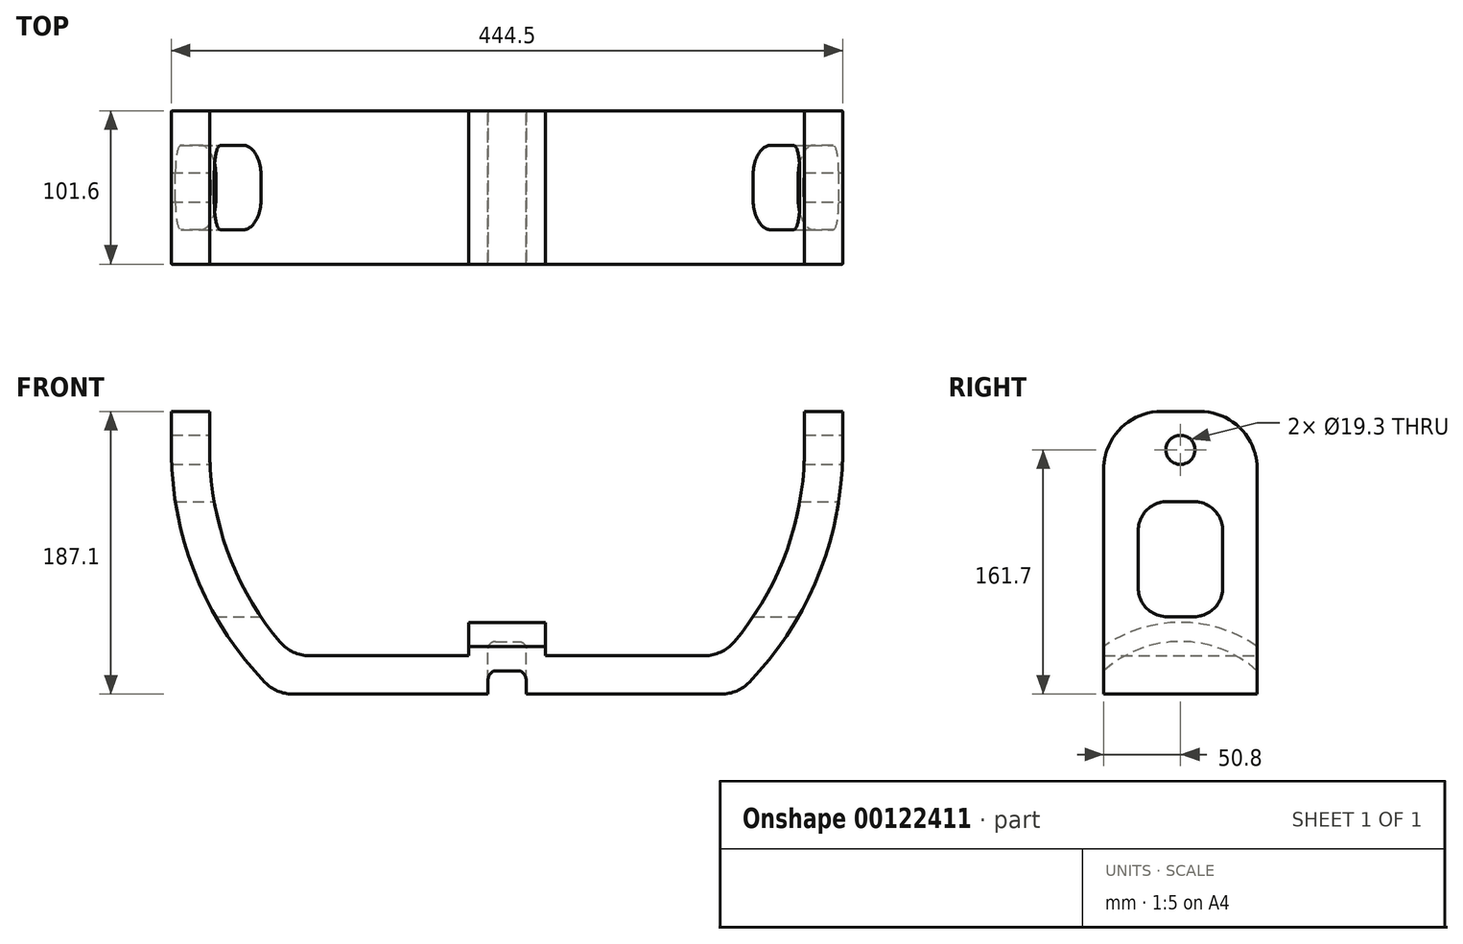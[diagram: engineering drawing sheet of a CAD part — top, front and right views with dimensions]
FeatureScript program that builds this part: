
annotation { "Feature Type Name" : "Feature", "Feature Type Description" : "" }
export const myFeature = defineFeature(function(context is Context, id is Id, definition is map)
    precondition{}
    {
        {
            var Q0;
            Q0=qCreatedBy(makeId("Front.planeOp"),FACE);
            var sketch = newSketch(context, id + "F0", { "sketchPlane" : qUnion([Q0])});
            skArc(sketch, "E0", {"start": v(-196.85, 0) * mm, "mid": v(-182.63, -73.46) * mm, "end": v(-142.03, -136.3) * mm});
            skArc(sketch, "E1.0", {"start": v(-222.25, 0) * mm, "mid": v(-204.06, -88.06) * mm, "end": v(-152.47, -161.7) * mm});
            skLineSegment(sketch, "E2", {"start": v(-196.85, 0) * mm, "end": v(196.85, 0) * mm, "construction": true});
            skLineSegment(sketch, "E3", {"start": v(-112.26, -161.7) * mm, "end": v(112.26, -161.7) * mm});
            skPoint(sketch, "E4", {"position": v(0, -161.7) * mm});
            skLineSegment(sketch, "E5.bottom", {"start": v(7.05, -253.9) * mm, "end": v(-7.05, -253.9) * mm, "construction": true});
            skLineSegment(sketch, "E5.top", {"start": v(7.05, -152.3) * mm, "end": v(-7.05, -152.3) * mm, "construction": true});
            skLineSegment(sketch, "E5.left", {"start": v(7.05, -253.9) * mm, "end": v(7.05, -152.3) * mm, "construction": true});
            skLineSegment(sketch, "E5.right", {"start": v(-7.05, -253.9) * mm, "end": v(-7.05, -152.3) * mm, "construction": true});
            skPoint(sketch, "E5.middle", {"position": v(0, -203.1) * mm});
            skCircle(sketch, "E6", {"center": v(0, 0) * mm, "radius": 254 * mm, "construction": true});
            skLineSegment(sketch, "E7.0", {"start": v(-142.03, -136.3) * mm, "end": v(142.03, -136.3) * mm});
            skLineSegment(sketch, "E8", {"start": v(-112.26, -161.7) * mm, "end": v(-152.47, -161.7) * mm});
            skLineSegment(sketch, "E9", {"start": v(112.26, -161.7) * mm, "end": v(152.47, -161.7) * mm});
            skArc(sketch, "E10.trimOffspring", {"start": v(142.03, -136.3) * mm, "mid": v(182.63, -73.46) * mm, "end": v(196.85, 0) * mm});
            skArc(sketch, "E11.trimOffspring", {"start": v(152.47, -161.7) * mm, "mid": v(204.06, -88.06) * mm, "end": v(222.25, 0) * mm});
            skLineSegment(sketch, "E12", {"start": v(-222.25, 0) * mm, "end": v(-222.25, 25.4) * mm});
            skLineSegment(sketch, "E13", {"start": v(-222.25, 25.4) * mm, "end": v(-196.85, 25.4) * mm});
            skLineSegment(sketch, "E14", {"start": v(-196.85, 25.4) * mm, "end": v(-196.85, 0) * mm});
            skLineSegment(sketch, "E15", {"start": v(196.85, 0) * mm, "end": v(196.85, 25.4) * mm});
            skLineSegment(sketch, "E16", {"start": v(196.85, 25.4) * mm, "end": v(222.25, 25.4) * mm});
            skLineSegment(sketch, "E17", {"start": v(222.25, 25.4) * mm, "end": v(222.25, 0) * mm});
            skLineSegment(sketch, "E18", {"start": v(0, 254) * mm, "end": v(0, -254) * mm, "construction": true});
            skSolve(sketch);
        }
        {
            var Q0;
            Q0 = qSketchRegion(id + "F0", true);
            extrude(context, id + "F1", {"entities" : qUnion([Q0]), "endBound" : BoundingType.SYMMETRIC, "depth" : 101.6 * mm, "offsetDistance" : 25.4 * mm});
        }
        {
            var Q0;
            Q0=makeQuery(id+"F1.opExtrude","SWEPT_EDGE",EDGE,{"disambiguationData":[OSD([sQuery(id+"F0.wireOp",EDGE,"E0"),sQuery(id+"F0.wireOp",EDGE,"E7.0")])]});
            var Q1;
            Q1=makeQuery(id+"F1.opExtrude","SWEPT_EDGE",EDGE,{"disambiguationData":[OSD([sQuery(id+"F0.wireOp",EDGE,"E1.0"),sQuery(id+"F0.wireOp",EDGE,"E8")])]});
            var Q2;
            Q2=makeQuery(id+"F1.opExtrude","SWEPT_EDGE",EDGE,{"disambiguationData":[OSD([sQuery(id+"F0.wireOp",EDGE,"E9"),sQuery(id+"F0.wireOp",EDGE,"E11.trimOffspring")])]});
            var Q3;
            Q3=makeQuery(id+"F1.opExtrude","SWEPT_EDGE",EDGE,{"disambiguationData":[OSD([sQuery(id+"F0.wireOp",EDGE,"E7.0"),sQuery(id+"F0.wireOp",EDGE,"E10.trimOffspring")])]});
            fillet(context, id + "F2", {"entities" : qUnion([Q0, Q1, Q2, Q3]), "tangentPropagation" : true, "radius" : 25.4 * mm, "defaultsChanged" : false, "vertexSettings" : [], "allowEdgeOverflow" : false});
        }
        {
            var Q0;
            Q0=makeQuery(id+"F1.opExtrude","CAP_EDGE",EDGE,{"disambiguationData":[OSD([sQuery(id+"F0.wireOp",EDGE,"E13")])],"isStart":false});
            var Q1;
            Q1=makeQuery(id+"F1.opExtrude","CAP_EDGE",EDGE,{"disambiguationData":[OSD([sQuery(id+"F0.wireOp",EDGE,"E13")])],"isStart":true});
            var Q2;
            Q2=makeQuery(id+"F1.opExtrude","CAP_EDGE",EDGE,{"disambiguationData":[OSD([sQuery(id+"F0.wireOp",EDGE,"E16")])],"isStart":true});
            var Q3;
            Q3=makeQuery(id+"F1.opExtrude","CAP_EDGE",EDGE,{"disambiguationData":[OSD([sQuery(id+"F0.wireOp",EDGE,"E16")])],"isStart":false});
            fillet(context, id + "F3", {"entities" : qUnion([Q0, Q1, Q2, Q3]), "tangentPropagation" : true, "radius" : 38.1 * mm, "defaultsChanged" : true, "vertexSettings" : [], "allowEdgeOverflow" : false});
        }
        {
            var Q0;
            Q0=qCreatedBy(makeId("Right.planeOp"),FACE);
            var sketch = newSketch(context, id + "F4", { "sketchPlane" : qUnion([Q0])});
            skCircle(sketch, "E19", {"center": v(0, 0) * mm, "radius": 9.65 * mm});
            skSolve(sketch);
        }
        {
            var Q0;
            Q0 = qSketchRegion(id + "F4", true);
            extrude(context, id + "F5", {"entities" : qUnion([Q0]), "operationType" : NewBodyOperationType.REMOVE, "endBound" : BoundingType.SYMMETRIC, "oppositeDirection" : true, "depth" : 482.6 * mm, "offsetDistance" : 25.4 * mm});
        }
        {
            var Q0;
            Q0=qCreatedBy(makeId("Right.planeOp"),FACE);
            var sketch = newSketch(context, id + "F6", { "sketchPlane" : qUnion([Q0])});
            skArc(sketch, "E20", {"start": v(50.8, -130.15) * mm, "mid": v(0, -114.2) * mm, "end": v(-50.8, -130.15) * mm});
            skArc(sketch, "E21", {"start": v(63.97, -161.7) * mm, "mid": v(0, -126.9) * mm, "end": v(-63.97, -161.7) * mm});
            skLineSegment(sketch, "E22.0", {"start": v(-50.8, -153.89) * mm, "end": v(-50.8, -130.15) * mm});
            skLineSegment(sketch, "E23.0", {"start": v(-50.8, -161.7) * mm, "end": v(-50.8, -153.89) * mm});
            skLineSegment(sketch, "E24.0", {"start": v(50.8, -161.7) * mm, "end": v(-50.8, -161.7) * mm});
            skLineSegment(sketch, "E25.0", {"start": v(50.8, -153.89) * mm, "end": v(50.8, -161.7) * mm});
            skLineSegment(sketch, "E26.0", {"start": v(50.8, -153.89) * mm, "end": v(50.8, -130.15) * mm});
            skPoint(sketch, "E27.orphan", {"position": v(-50.8, -12.7) * mm});
            skPoint(sketch, "E28.orphan", {"position": v(50.8, -12.7) * mm});
            skSolve(sketch);
        }
        {
            var Q0;
            Q0=qCreatedBy(makeId("Right.planeOp"),FACE);
            var sketch = newSketch(context, id + "F7", { "sketchPlane" : qUnion([Q0])});
            skArc(sketch, "E29.0", {"start": v(50.8, -130.15) * mm, "mid": v(0, -114.2) * mm, "end": v(-50.8, -130.15) * mm});
            skLineSegment(sketch, "E30.0", {"start": v(-50.8, -153.89) * mm, "end": v(-50.8, -130.15) * mm});
            skLineSegment(sketch, "E31.0", {"start": v(-50.8, -161.7) * mm, "end": v(-50.8, -153.89) * mm});
            skLineSegment(sketch, "E32.0", {"start": v(50.8, -161.7) * mm, "end": v(-50.8, -161.7) * mm});
            skLineSegment(sketch, "E33.0", {"start": v(50.8, -153.89) * mm, "end": v(50.8, -130.15) * mm});
            skLineSegment(sketch, "E34.0", {"start": v(50.8, -153.89) * mm, "end": v(50.8, -161.7) * mm});
            skSolve(sketch);
        }
        {
            var Q0;
            Q0 = qSketchRegion(id + "F7", true);
            extrude(context, id + "F8", {"entities" : qUnion([Q0]), "operationType" : NewBodyOperationType.ADD, "endBound" : BoundingType.SYMMETRIC, "depth" : 50.8 * mm, "offsetDistance" : 25.4 * mm});
        }
        {
            var Q0;
            Q0=qCreatedBy(makeId("Right.planeOp"),FACE);
            var sketch = newSketch(context, id + "F9", { "sketchPlane" : qUnion([Q0])});
            skArc(sketch, "E35.0", {"start": v(63.97, -161.7) * mm, "mid": v(0, -126.9) * mm, "end": v(-63.97, -161.7) * mm});
            skLineSegment(sketch, "E36.0", {"start": v(50.8, -161.7) * mm, "end": v(-50.8, -161.7) * mm});
            skLineSegment(sketch, "E37", {"start": v(-63.97, -161.7) * mm, "end": v(-50.8, -161.7) * mm});
            skLineSegment(sketch, "E38", {"start": v(50.8, -161.7) * mm, "end": v(63.97, -161.7) * mm});
            skSolve(sketch);
        }
        {
            var Q0;
            Q0 = qSketchRegion(id + "F9", true);
            extrude(context, id + "F10", {"entities" : qUnion([Q0]), "operationType" : NewBodyOperationType.REMOVE, "endBound" : BoundingType.SYMMETRIC, "oppositeDirection" : true, "depth" : 25.4 * mm, "offsetDistance" : 25.4 * mm});
        }
        {
            var Q0;
            Q0=qCreatedBy(makeId("Right.planeOp"),FACE);
            var sketch = newSketch(context, id + "F11", { "sketchPlane" : qUnion([Q0])});
            skLineSegment(sketch, "E39.bottom", {"start": v(8.89, -110.5) * mm, "end": v(-8.9, -110.5) * mm});
            skLineSegment(sketch, "E39.top", {"start": v(8.9, -34.3) * mm, "end": v(-8.9, -34.3) * mm});
            skLineSegment(sketch, "E39.left", {"start": v(27.94, -91.44) * mm, "end": v(27.94, -53.34) * mm});
            skLineSegment(sketch, "E39.right", {"start": v(-27.94, -91.44) * mm, "end": v(-27.94, -53.34) * mm});
            skPoint(sketch, "E39.middle", {"position": v(0, -72.4) * mm});
            skPoint(sketch, "E40.visualSharp", {"position": v(-27.94, -34.3) * mm});
            skArc(sketch, "E40.filletArc", {"start": v(-8.89, -34.3) * mm, "mid": v(-22.36, -39.87) * mm, "end": v(-27.94, -53.34) * mm});
            skPoint(sketch, "E41.visualSharp", {"position": v(27.94, -34.3) * mm});
            skArc(sketch, "E41.filletArc", {"start": v(27.94, -53.34) * mm, "mid": v(22.36, -39.87) * mm, "end": v(8.9, -34.3) * mm});
            skPoint(sketch, "E42.visualSharp", {"position": v(-27.94, -110.5) * mm});
            skArc(sketch, "E42.filletArc", {"start": v(-27.94, -91.44) * mm, "mid": v(-22.36, -104.91) * mm, "end": v(-8.9, -110.49) * mm});
            skPoint(sketch, "E43.visualSharp", {"position": v(27.94, -110.5) * mm});
            skArc(sketch, "E43.filletArc", {"start": v(8.89, -110.49) * mm, "mid": v(22.36, -104.91) * mm, "end": v(27.94, -91.44) * mm});
            skSolve(sketch);
        }
        {
            var Q0;
            Q0 = qSketchRegion(id + "F11", true);
            extrude(context, id + "F12", {"entities" : qUnion([Q0]), "operationType" : NewBodyOperationType.REMOVE, "endBound" : BoundingType.SYMMETRIC, "oppositeDirection" : true, "depth" : 558.8 * mm, "offsetDistance" : 25.4 * mm});
        }
        {
            var Q0;
            Q0=makeQuery(id+"F10.boolean.opBoolean","COPY",EDGE,{"derivedFrom":makeQuery(id+"F10.opExtrude","CAP_EDGE",EDGE,{"disambiguationData":[OSD([sQuery(id+"F9.wireOp",EDGE,"E35.0")])],"isStart":false})});
            var Q1;
            Q1=makeQuery(id+"F10.boolean.opBoolean","COPY",EDGE,{"derivedFrom":makeQuery(id+"F10.opExtrude","CAP_EDGE",EDGE,{"disambiguationData":[OSD([sQuery(id+"F9.wireOp",EDGE,"E35.0")])],"isStart":true})});
            fillet(context, id + "F13", {"entities" : qUnion([Q0, Q1]), "tangentPropagation" : true, "radius" : 5.08 * mm, "defaultsChanged" : false, "vertexSettings" : [], "allowEdgeOverflow" : false});
        }
    });
